# Revit family: NEVD
name_source: partatom
category: Lighting Fixtures
revit_build: Autodesk Revit 2014 (Build: 20130308_1515(x64)
units: mm (PartAtom-declared; Revit-internal decimal feet)

## types (1)
- NEVD
    Apparent Load = 50 VA
    Assembly Code = D5020200
    Color Filter = 16777215
    Connector Description = Lighting Connector
    Default Elevation = 1219.2 mm  [stored 4 ft]
    Description = The Nevis bulkhead is designed for low profile applications. It can be mounted on walls, handrails and ceilings making it ideal for walkways or restricted height areas. The wide ambient temperature range makes the Nevis suitable for extreme environmental conditions. The luminaire is suitable for high pressure discharge lamps up to 70W HPS and compact fluorescent lamps up to 26W. The large side mounted increased safety terminal chamber eliminates the need for flameproof glands and allows for flush mounting with easy cable access. The ATEX rated bulkhead suitable for Zone 1 and Zone 21 applications is made from corrosion resistant aluminium alloy and toughened boro-silicate glass using stainless steel fastenings.
    Dimming Lamp Color Temperature Shift = <None>
    Emit Shape Visible in Rendering = No
    Emit from Circle Diameter = 50 mm  [stored 0.164042 ft]
    Features = Installation to gas groups IIA and IIB.
Ex e cable entries and looping as standard.
Hinged front cover.
Captive cover screws.
High ingress protection.
Internal reflector options.
Low temperature applications to -55˚C.
Compact construction.
    Fixture distribution = Direct
    Glass = Hubbell - Glass
    Height = 535 mm
    Housing Material = Paint - Hubbell - Gray Smooth
    IP Rating = IP66/67
    Inner Length = 200 mm  [stored 0.656168 ft]
    Lamp = LED
    Length = 245 mm  [stored 0.803806 ft]
    Load Classification = Lighting
    Manufacturer = Chalmit
    Model = NEVD
    Mounting = Paint - Hubbell - Light Silver
    Photometric Web File = CHL_NEVD_050_HS.ies
    Power Factor = 1
    Product Documentation Link = https://hubbellcdn.com
    Product Link = https://www.hubbell.com
    Reflector Finish = Hubbell - White Glass
    Tilt Angle = 90.00°
    URL = https://www.hubbell.com
    Voltage = 120 V
    Warranty = 5 years Warranty
    Wattage Comments = 50W
    Watts = 50 W
    Width = 280 mm  [stored 0.918635 ft]
    Wings = Paint - Hubbell - Light Silver

note: [stored X ft] marks values corroborated as IEEE doubles in the binary element streams (Revit-internal decimal feet)

## geometry (parser evidence)
native form markers: Sweep x4
no freeform markers — native parametric forms only
